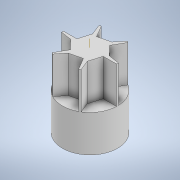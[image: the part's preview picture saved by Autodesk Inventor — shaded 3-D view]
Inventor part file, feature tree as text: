
AUTODESK INVENTOR PART (.ipt)
format: ipt  version: 2021 (Build 250183000, 183)  size: 123,392 bytes
history: native  units: in
note: dims shown in document units (in); Inventor stores cm internally (conversion verified against a paired STEP export)
features: extrude x2, sketch x2, pattern_circular x1
ambient origin geometry x8: Origin, YZ Plane, XZ Plane, XY Plane, X Axis, Y Axis, Z Axis, Center Point
bodies: Solid1 (feature_tree)
feature tree (5):
  extrude  "Extrusion1"  Depth=1.0in TaperAngle=0.0deg
  extrude  "Extrusion2"  Depth=0.5in TaperAngle=360.0deg
  pattern_circular  "Circular Pattern1"  [2 undecoded]
  sketch  "Sketch1"  dims[d0=0.75in d1=1.0in d2=0.0in]
  sketch  "Sketch2"  dims[d3=0.5in d4=0.0in d5=2.3622in d6=360.0deg]
note: 2 required parameter values undecoded (feature->parameter linkage not recoverable at this tier; creation-order binding heuristic only, values carry confidence <= 0.55)
